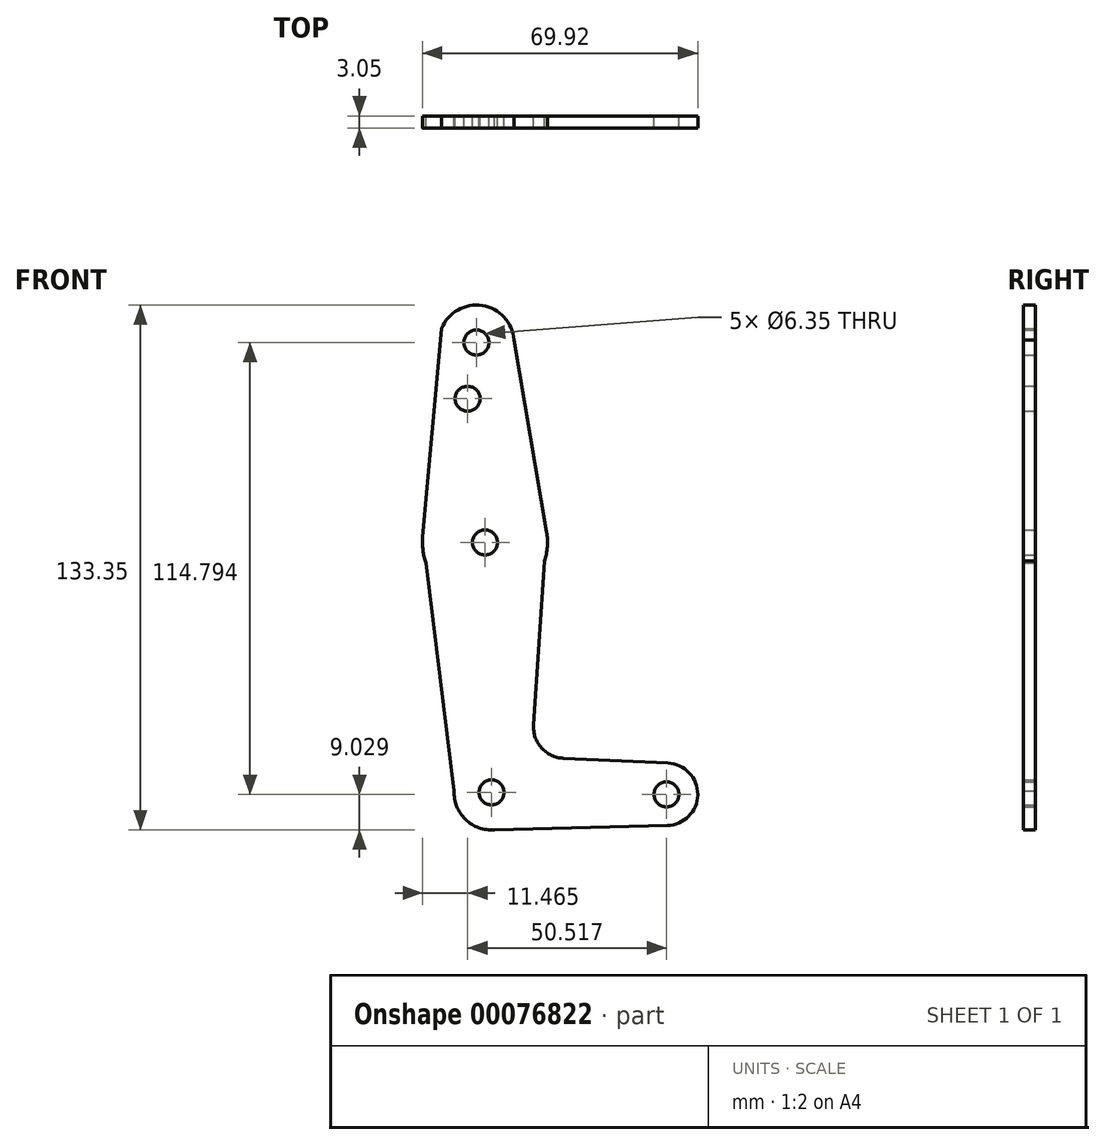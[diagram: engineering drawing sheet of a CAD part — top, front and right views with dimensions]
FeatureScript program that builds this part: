
annotation { "Feature Type Name" : "Feature", "Feature Type Description" : "" }
export const myFeature = defineFeature(function(context is Context, id is Id, definition is map)
    precondition{}
    {
        {
            var Q0;
            Q0=qCreatedBy(makeId("Front.planeOp"),FACE);
            var sketch = newSketch(context, id + "F0", { "sketchPlane" : qUnion([Q0])});
            skCircle(sketch, "E0", {"center": v(-259.84, 268.67) * mm, "radius": 7.94 * mm});
            skCircle(sketch, "E1", {"center": v(-304.28, 269.16) * mm, "radius": 9.53 * mm});
            skCircle(sketch, "E2", {"center": v(-305.95, 332.66) * mm, "radius": 15.88 * mm});
            skCircle(sketch, "E3", {"center": v(-308.13, 383.46) * mm, "radius": 9.53 * mm});
            skLineSegment(sketch, "E4", {"start": v(-259.84, 268.67) * mm, "end": v(-304.28, 269.16) * mm, "construction": true});
            skLineSegment(sketch, "E5", {"start": v(-286.03, 277.83) * mm, "end": v(-259.47, 276.6) * mm});
            skLineSegment(sketch, "E6", {"start": v(-303.56, 259.67) * mm, "end": v(-259.64, 260.73) * mm});
            skCircle(sketch, "E7", {"center": v(-308.13, 383.46) * mm, "radius": 3.18 * mm});
            skLineSegment(sketch, "E8", {"start": v(-316.99, 386.98) * mm, "end": v(-321.76, 334.09) * mm});
            skLineSegment(sketch, "E9", {"start": v(-298.63, 384.1) * mm, "end": v(-290.3, 335.34) * mm});
            skLineSegment(sketch, "E10", {"start": v(-313.8, 269.5) * mm, "end": v(-321.76, 334.09) * mm});
            skLineSegment(sketch, "E11", {"start": v(-290.3, 335.34) * mm, "end": v(-293.6, 286.3) * mm});
            skLineSegment(sketch, "E12", {"start": v(-308.13, 383.46) * mm, "end": v(-304.28, 269.16) * mm, "construction": true});
            skCircle(sketch, "E13", {"center": v(-310.35, 369.19) * mm, "radius": 3.18 * mm});
            skCircle(sketch, "E14", {"center": v(-305.95, 332.66) * mm, "radius": 3.18 * mm});
            skCircle(sketch, "E15", {"center": v(-304.28, 269.16) * mm, "radius": 3.18 * mm});
            skCircle(sketch, "E16", {"center": v(-259.84, 268.67) * mm, "radius": 3.18 * mm});
            skArc(sketch, "E17.filletArc", {"start": v(-293.6, 286.3) * mm, "mid": v(-291.6, 280.48) * mm, "end": v(-286.03, 277.83) * mm});
            skSolve(sketch);
        }
        {
            var Q0;
            {var subQ0=sQuery(id+"F0.wireOp",EDGE,"E10");var subQ1=sQuery(id+"F0.wireOp",EDGE,"E2");var subQ3=makeQuery(id+"F0.imprint","INTERSECT",VERTEX,{"derivedFrom":[subQ1,subQ0]});Q0=makeQuery(id+"F0.imprint","IMPRINT",FACE,{"disambiguationData":[TD([[makeQuery(id+"F0.imprint","IMPRINT",EDGE,{"disambiguationData":[TD([[subQ3,1.0]])],"derivedFrom":subQ1}),1.0]])]});}
            var Q1;
            {var subQ0=sQuery(id+"F0.wireOp",EDGE,"E11");var subQ1=sQuery(id+"F0.wireOp",EDGE,"E2");var subQ3=makeQuery(id+"F0.imprint","INTERSECT",VERTEX,{"derivedFrom":[subQ1,subQ0]});Q1=makeQuery(id+"F0.imprint","IMPRINT",FACE,{"disambiguationData":[TD([[makeQuery(id+"F0.imprint","IMPRINT",EDGE,{"disambiguationData":[TD([[subQ3,-1.0]])],"derivedFrom":subQ1}),1.0]])]});}
            var Q2;
            {var subQ0=sQuery(id+"F0.wireOp",EDGE,"E8");var subQ1=sQuery(id+"F0.wireOp",EDGE,"E3");var subQ2=makeQuery(id+"F0.imprint","INTERSECT",VERTEX,{"disambiguationData":[OD(0.0)],"derivedFrom":[subQ1,subQ0]});Q2=makeQuery(id+"F0.imprint","IMPRINT",FACE,{"disambiguationData":[TD([[makeQuery(id+"F0.imprint","IMPRINT",EDGE,{"disambiguationData":[TD([[subQ2,-1.0]])],"derivedFrom":subQ1}),1.0]])]});}
            var Q3;
            Q3=makeQuery(id+"F0.imprint","IMPRINT",FACE,{"disambiguationData":[TD([[makeQuery(id+"F0.imprint","IMPRINT",EDGE,{"derivedFrom":sQuery(id+"F0.wireOp",EDGE,"E16")}),-1.0]])]});
            var Q4;
            Q4=makeQuery(id+"F0.imprint","IMPRINT",FACE,{"disambiguationData":[TD([[makeQuery(id+"F0.imprint","IMPRINT",EDGE,{"derivedFrom":sQuery(id+"F0.wireOp",EDGE,"E15")}),-1.0]])]});
            var Q5;
            {var subQ0=sQuery(id+"F0.wireOp",EDGE,"E5");Q5=makeQuery(id+"F0.imprint","IMPRINT",FACE,{"disambiguationData":[TD([[makeQuery(id+"F0.imprint","IMPRINT",EDGE,{"derivedFrom":subQ0}),-1.0]])]});}
            var Q6;
            {var subQ0=sQuery(id+"F0.wireOp",EDGE,"E9");Q6=makeQuery(id+"F0.imprint","IMPRINT",FACE,{"disambiguationData":[TD([[makeQuery(id+"F0.imprint","IMPRINT",EDGE,{"derivedFrom":subQ0}),-1.0]])]});}
            var Q7;
            Q7=makeQuery(id+"F0.imprint","IMPRINT",FACE,{"disambiguationData":[TD([[makeQuery(id+"F0.imprint","IMPRINT",EDGE,{"derivedFrom":sQuery(id+"F0.wireOp",EDGE,"E7")}),-1.0]])]});
            var Q8;
            Q8=makeQuery(id+"F0.imprint","IMPRINT",FACE,{"disambiguationData":[TD([[makeQuery(id+"F0.imprint","IMPRINT",EDGE,{"derivedFrom":sQuery(id+"F0.wireOp",EDGE,"E14")}),-1.0]])]});
            extrude(context, id + "F1", {"entities" : qUnion([Q0, Q1, Q2, Q3, Q4, Q5, Q6, Q7, Q8]), "depth" : 3.05 * mm});
        }
    });
